# Revit family: Перегородка ППО-60
name_source: partatom
category: Двери
revit_build: Autodesk Revit 2017 (Build: 20160225_1515(x64)
units: mm (PartAtom-declared; Revit-internal decimal feet)

## family parameters
Всегда вертикально = Да
Заголовок OmniClass = Doors
Номер OmniClass = 23.30.10.00
Общий = Нет
Основа = Стена
При загрузке вырезать с полостями = Нет
Точка расчета площади = Нет

## types (4) — shared parameters
3 петли = 1
3петли = Да
ADSK_URL страницы изделия = http://www.dwrcenter.ru
ADSK_Завод-изготовитель = ДВР Центр, г.Москва
ADSK_Наименование = ППО-ОГНЕДЕКОР-60
ADSK_Наименование краткое = ППО-60
ADSK_Обозначение = ГОСТ Р 53308-2009
ADSK_Предел огнестойкости = EIW-60
URL = http://dwrcenter.ru
Высота = 3000 мм
Высота двери = 2200 мм
Высота импоста = 1050 мм
Высота стекла боковины = 1122 мм
Высота стекла двери = 1122 мм
Высота фрамуги = 790 мм
Габаритная ширина створки = 1578 мм
Группа модели = Остекленные противопожарные конструкции
Замыкание стены = По основе
Заполнение зазора = Да
Изготовитель = ДВР Центр, г.Москва
Импост = Да
Материал нижней вставки = <По категории>
Материал стеклопакета = Стекло
Материал_коробки = <По категории>
Материал_створки = <По категории>
Монтажный зазор сверху = 10 мм
Монтажный зазор слева = 10 мм
Монтажный зазор справа = 10 мм
Наличник внутри = Да
Наличник снаружи = Да
Огнестойкость = EIW-60
Описание = Перегородка противопожарная остекленная
Телефоны изготовителя = +7-495-4-112-911, +7-495-5-103-206
Тип конструкций = Перегородка противопожарная остекленная, ГОСТ Р 53308-2009
Толщина = 50 мм
Функция = Внутренние слои
Цвет доводчика = Сталь нержавеющая
Цвет наличника с внутренней стороны = Отделка. Орех
Цвет наличника снаружи = Отделка. Орех
Цвет петли = Сталь нержавеющая
Цвет фурнитуры = Сталь нержавеющая
Ширина С1 = 762 мм
Ширина С2 = 762 мм
Ширина двери = 1600 мм
Ширина левой створки = 722 мм
Ширина наличника = 60 мм
Ширина правой створки = 722 мм
Ширина створок при равнопольной двери = 722 мм
zero-valued in all types: ADSK_Количество, ADSK_Откосы_Глубина, ADSK_Толщина стены, ADSK_Толщина стены (отчет)

## per-type parameters (varying)
| type | ADSK_Открывание | Глубина вставки двери | Заполнение монтажного зазора | Левая | Правая | Ширина | Ширина левой фрамуги | Ширина правой фрамуги |
| ППО-ОГНЕДЕКОР-60, правая, 3000х3000 | Правая | 0 мм | Пена монтажная | Нет | Да | 3000 мм | 690 мм | 690 мм |
| ППО-ОГНЕДЕКОР-60, левая, 3000х3000 | Левая | 20 мм | <По категории> | Да | Нет | 3000 мм | 690 мм | 690 мм |
| ППО-ОГНЕДЕКОР-60, правая, 3500х3000 | Правая | 0 мм | Пена монтажная | Нет | Да | 3500 мм | 940 мм | 940 мм |
| ППО-ОГНЕДЕКОР-60, левая, 3500х3000 | Левая | 0 мм | Пена монтажная | Да | Нет | 3500 мм | 940 мм | 940 мм |
